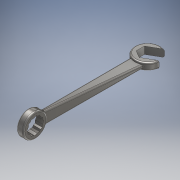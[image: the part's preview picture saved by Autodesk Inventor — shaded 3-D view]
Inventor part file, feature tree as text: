
AUTODESK INVENTOR PART (.ipt)
format: ipt  version: 2018 (Build 220112000, 112)  size: 322,560 bytes
history: native  units: mm
features: other x8, extrude x4, sketch x2, loft x1, fillet x1
ambient origin geometry x8: Origin, YZ Plane, XZ Plane, XY Plane, X Axis, Y Axis, Z Axis, Center Point
bodies: Solid1 (feature_tree)
feature tree (16):
  other  "Table"
  other  "Wrench-01"
  other  "Wrench-02"
  other  "Wrench-03"
  other  "Wrench-04"
  other  "Wrench-05"
  sketch  "Sketch1"  dims[d1=35.0mm d2=60.0deg]
  extrude  "Extrusion1"  TaperAngle=60.0deg  [1 undecoded]
  sketch  "Sketch4"  dims[d3=5.0mm d4=0.0mm d5=160.0mm d6=20.0mm d7=0.0mm d8=25.261129mm d9=33.0mm d10=5.0mm d11=0.0mm d13=20.0mm d14=5.0mm d15=0.0mm d16=20.0mm d17=5.0mm d18=0.0mm d19=0.0mm d20=90.0deg d21=0.0mm d22=90.0deg d23=10.0mm d24=0.0mm d25=10.0mm d26=0.0mm d27=2.0mm]
  extrude  "Extrusion2"  TaperAngle=0.0deg  [1 undecoded]
  loft  "Loft1"
  extrude  "Extrusion3"  Depth=2.0mm
  extrude  "Extrusion4"  TaperAngle=0.0deg  [1 undecoded]
  fillet  "Fillet1"  Radius=25.261129mm
  other  "Edges1"
  other  "Edges2"
note: 3 required parameter values undecoded (feature->parameter linkage not recoverable at this tier; creation-order binding heuristic only, values carry confidence <= 0.55)
